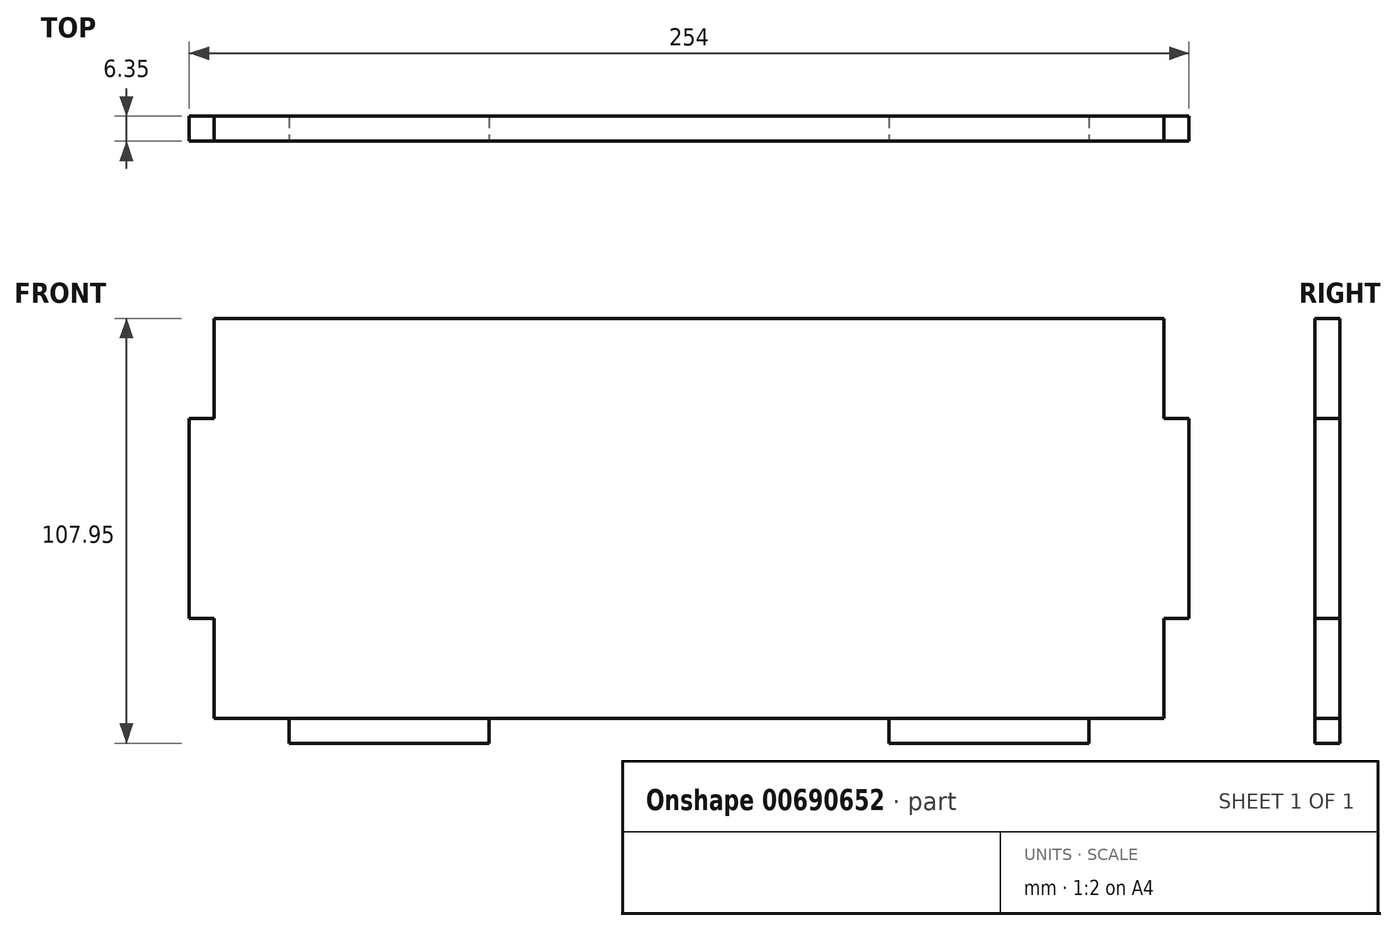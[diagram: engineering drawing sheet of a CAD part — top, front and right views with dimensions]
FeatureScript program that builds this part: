
annotation { "Feature Type Name" : "Feature", "Feature Type Description" : "" }
export const myFeature = defineFeature(function(context is Context, id is Id, definition is map)
    precondition{}
    {
        {
            var Q0;
            Q0=qCreatedBy(makeId("Front.planeOp"),FACE);
            var sketch = newSketch(context, id + "F0", { "sketchPlane" : qUnion([Q0])});
            skLineSegment(sketch, "E0.bottom", {"start": v(-127, 101.6) * mm, "end": v(127, 101.6) * mm});
            skLineSegment(sketch, "E0.top", {"start": v(-127, 0) * mm, "end": v(127, 0) * mm});
            skLineSegment(sketch, "E0.left", {"start": v(-127, 101.6) * mm, "end": v(-127, 0) * mm});
            skLineSegment(sketch, "E0.right", {"start": v(127, 101.6) * mm, "end": v(127, 0) * mm});
            skSolve(sketch);
        }
        {
            var Q0;
            Q0 = qSketchRegion(id + "F0", true);
            extrude(context, id + "F1", {"entities" : qUnion([Q0]), "depth" : 6.35 * mm, "offsetDistance" : 25.4 * mm});
        }
        {
            var Q0;
            Q0=makeQuery(id+"F1.opExtrude","CAP_FACE",FACE,{"disambiguationData":[OSD([sQuery(id+"F0.wireOp",EDGE,"E0.bottom"),sQuery(id+"F0.wireOp",EDGE,"E0.top"),sQuery(id+"F0.wireOp",EDGE,"E0.left"),sQuery(id+"F0.wireOp",EDGE,"E0.right")])],"isStart":false});
            var sketch = newSketch(context, id + "F2", { "sketchPlane" : qUnion([Q0])});
            skLineSegment(sketch, "E1.bottom", {"start": v(101.6, 0) * mm, "end": v(50.8, 0) * mm});
            skLineSegment(sketch, "E1.top", {"start": v(101.6, -6.35) * mm, "end": v(50.8, -6.35) * mm});
            skLineSegment(sketch, "E1.left", {"start": v(101.6, -6.35) * mm, "end": v(101.6, 0) * mm});
            skLineSegment(sketch, "E1.right", {"start": v(50.8, -6.35) * mm, "end": v(50.8, 0) * mm});
            skLineSegment(sketch, "E2.MirrorCS", {"start": v(-101.6, 0) * mm, "end": v(-50.8, 0) * mm});
            skLineSegment(sketch, "E3.MirrorCS", {"start": v(-101.6, -6.35) * mm, "end": v(-50.8, -6.35) * mm});
            skLineSegment(sketch, "E4.MirrorCS", {"start": v(-101.6, -6.35) * mm, "end": v(-101.6, 0) * mm});
            skLineSegment(sketch, "E5.MirrorCS", {"start": v(-50.8, -6.35) * mm, "end": v(-50.8, 0) * mm});
            skSolve(sketch);
        }
        {
            var Q0;
            Q0 = qSketchRegion(id + "F2", true);
            extrude(context, id + "F3", {"entities" : qUnion([Q0]), "oppositeDirection" : true, "depth" : 6.35 * mm, "offsetDistance" : 25.4 * mm});
        }
        {
            var Q0;
            Q0=makeQuery(id+"F1.opExtrude","CAP_FACE",FACE,{"disambiguationData":[OSD([sQuery(id+"F0.wireOp",EDGE,"E0.bottom"),sQuery(id+"F0.wireOp",EDGE,"E0.top"),sQuery(id+"F0.wireOp",EDGE,"E0.left"),sQuery(id+"F0.wireOp",EDGE,"E0.right")])],"isStart":false});
            var sketch = newSketch(context, id + "F4", { "sketchPlane" : qUnion([Q0])});
            skLineSegment(sketch, "E6.bottom", {"start": v(127, 101.6) * mm, "end": v(120.65, 101.6) * mm});
            skLineSegment(sketch, "E6.top", {"start": v(127, 76.2) * mm, "end": v(120.65, 76.2) * mm});
            skLineSegment(sketch, "E6.left", {"start": v(127, 101.6) * mm, "end": v(127, 76.2) * mm});
            skLineSegment(sketch, "E6.right", {"start": v(120.65, 101.6) * mm, "end": v(120.65, 76.2) * mm});
            skLineSegment(sketch, "E7.bottom", {"start": v(127, 0) * mm, "end": v(120.65, 0) * mm});
            skLineSegment(sketch, "E7.top", {"start": v(127, 25.4) * mm, "end": v(120.65, 25.4) * mm});
            skLineSegment(sketch, "E7.left", {"start": v(127, 0) * mm, "end": v(127, 25.4) * mm});
            skLineSegment(sketch, "E7.right", {"start": v(120.65, 0) * mm, "end": v(120.65, 25.4) * mm});
            skLineSegment(sketch, "E8.MirrorCS", {"start": v(-120.65, 0) * mm, "end": v(-120.65, 25.4) * mm});
            skLineSegment(sketch, "E9.MirrorCS", {"start": v(-127, 0) * mm, "end": v(-127, 25.4) * mm});
            skLineSegment(sketch, "E10.MirrorCS", {"start": v(-127, 25.4) * mm, "end": v(-120.65, 25.4) * mm});
            skLineSegment(sketch, "E11.MirrorCS", {"start": v(-127, 101.6) * mm, "end": v(-120.65, 101.6) * mm});
            skLineSegment(sketch, "E12.MirrorCS", {"start": v(-127, 76.2) * mm, "end": v(-120.65, 76.2) * mm});
            skLineSegment(sketch, "E13.MirrorCS", {"start": v(-127, 101.6) * mm, "end": v(-127, 76.2) * mm});
            skLineSegment(sketch, "E14.MirrorCS", {"start": v(-127, 0) * mm, "end": v(-120.65, 0) * mm});
            skLineSegment(sketch, "E15.MirrorCS", {"start": v(-120.65, 101.6) * mm, "end": v(-120.65, 76.2) * mm});
            skSolve(sketch);
        }
        {
            var Q0;
            Q0 = qSketchRegion(id + "F4", true);
            extrude(context, id + "F5", {"entities" : qUnion([Q0]), "operationType" : NewBodyOperationType.REMOVE, "oppositeDirection" : true, "depth" : 25.4 * mm, "offsetDistance" : 25.4 * mm});
        }
    });
